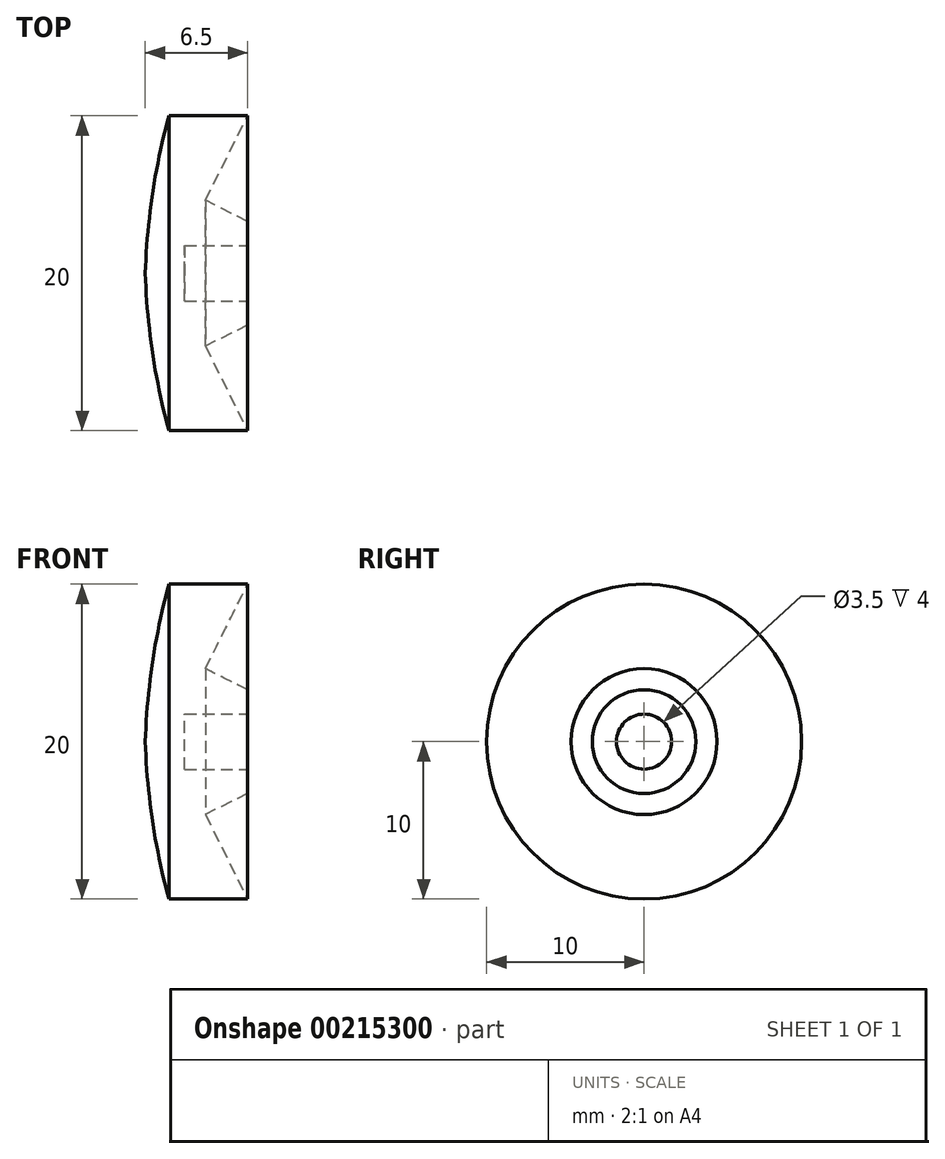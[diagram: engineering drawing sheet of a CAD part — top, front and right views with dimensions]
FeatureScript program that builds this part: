
annotation { "Feature Type Name" : "Feature", "Feature Type Description" : "" }
export const myFeature = defineFeature(function(context is Context, id is Id, definition is map)
    precondition{}
    {
        {
            var Q0;
            Q0=qCreatedBy(makeId("Top.planeOp"),FACE);
            var sketch = newSketch(context, id + "F0", { "sketchPlane" : qUnion([Q0])});
            skLineSegment(sketch, "E0", {"start": v(0, 10) * mm, "end": v(5, 10) * mm});
            skLineSegment(sketch, "E1", {"start": v(5, 10) * mm, "end": v(2.32, 4.63) * mm});
            skLineSegment(sketch, "E2", {"start": v(2.32, 4.63) * mm, "end": v(5, 3.3) * mm});
            skLineSegment(sketch, "E3", {"start": v(5, 3.3) * mm, "end": v(5, 0) * mm});
            skArc(sketch, "E4", {"start": v(0, 10) * mm, "mid": v(-1.04, 5.04) * mm, "end": v(-1.5, 0) * mm});
            skPoint(sketch, "E5.start.orphan", {"position": v(0, 0) * mm});
            skPoint(sketch, "E6.start.orphan", {"position": v(-4.12, 0) * mm});
            skLineSegment(sketch, "E7", {"start": v(-1.5, 0) * mm, "end": v(5, 0) * mm});
            skLineSegment(sketch, "E8", {"start": v(-4.12, 0) * mm, "end": v(7.36, 0) * mm, "construction": true});
            skPoint(sketch, "E8.endSnap0", {"position": v(1.75, 0) * mm});
            skSolve(sketch);
        }
        {
            var Q0;
            Q0=makeQuery(id+"F0.imprint","IMPRINT",FACE,{"disambiguationData":[TD([[makeQuery(id+"F0.imprint","IMPRINT",EDGE,{"derivedFrom":sQuery(id+"F0.wireOp",EDGE,"E0")}),-1.0]])]});
            var Q1;
            Q1=sQuery(id+"F0.wireOp",EDGE,"E8");
            revolve(context, id + "F1", {"entities" : qUnion([Q0]), "axis" : qUnion([Q1]), "revolveType" : RevolveType.FULL});
        }
        {
            var Q0;
            Q0=makeQuery(id+"F1.opRevolve","SWEPT_FACE",FACE,{"disambiguationData":[OSD([sQuery(id+"F0.wireOp",EDGE,"E3")])]});
            var sketch = newSketch(context, id + "F2", { "sketchPlane" : qUnion([Q0])});
            skCircle(sketch, "E9", {"center": v(0, 0) * mm, "radius": 1.75 * mm});
            skSolve(sketch);
        }
        {
            var Q0;
            Q0=makeQuery(id+"F2.imprint","IMPRINT",FACE,{"disambiguationData":[TD([[makeQuery(id+"F2.imprint","IMPRINT",EDGE,{"derivedFrom":sQuery(id+"F2.wireOp",EDGE,"E9")}),1.0]])]});
            extrude(context, id + "F3", {"entities" : qUnion([Q0]), "operationType" : NewBodyOperationType.REMOVE, "oppositeDirection" : true, "depth" : 4 * mm});
        }
    });
